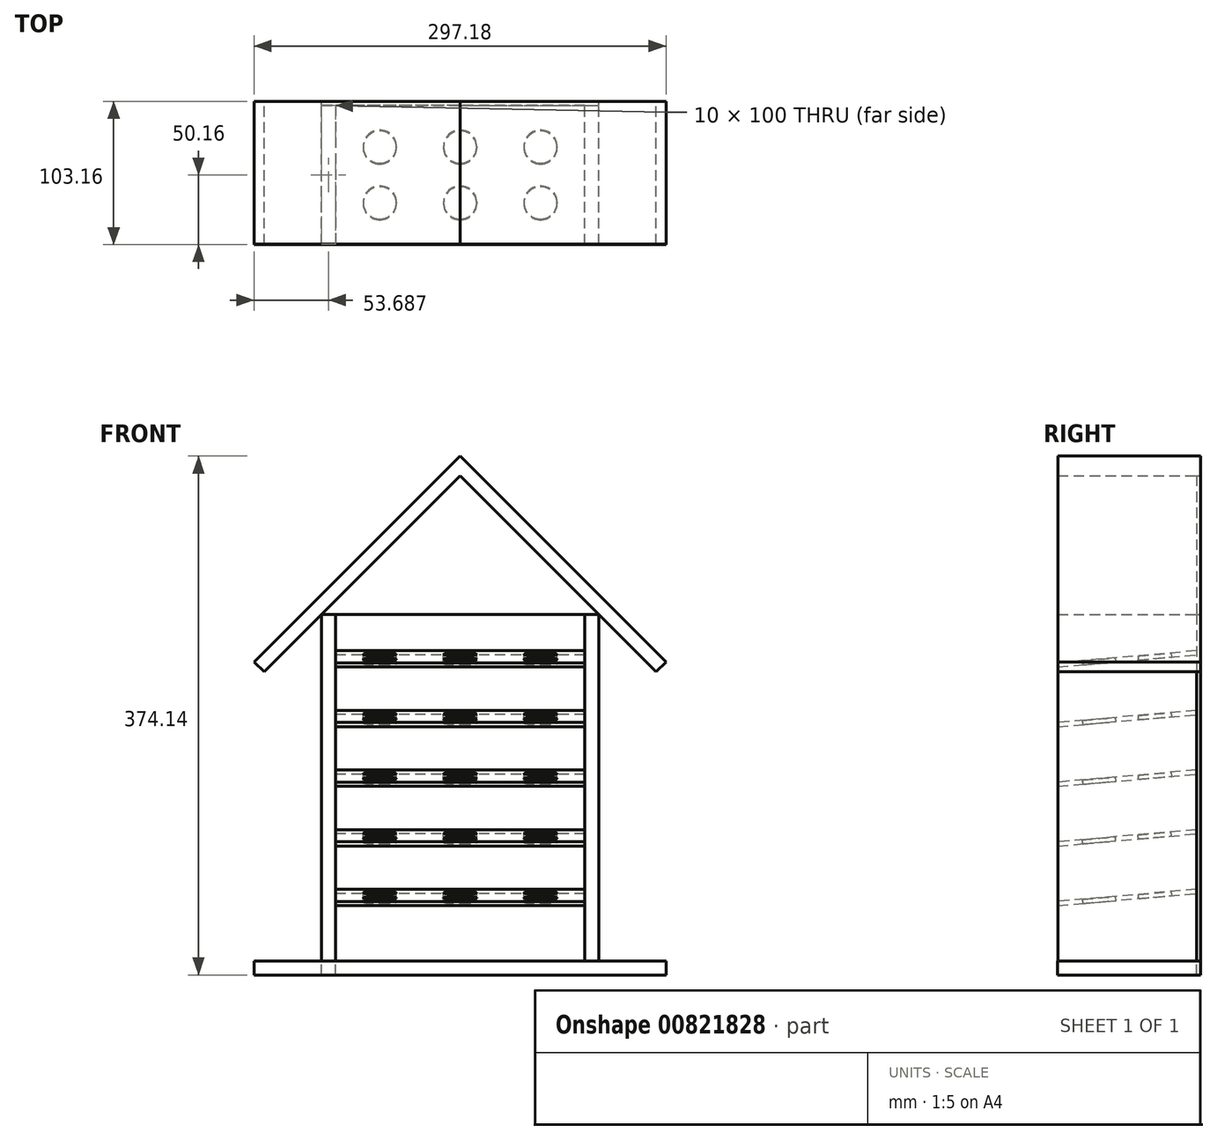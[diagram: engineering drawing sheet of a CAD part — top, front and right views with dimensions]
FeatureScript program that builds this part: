
annotation { "Feature Type Name" : "Feature", "Feature Type Description" : "" }
export const myFeature = defineFeature(function(context is Context, id is Id, definition is map)
    precondition{}
    {
        {
            var Q0;
            Q0=qCreatedBy(makeId("Front.planeOp"),FACE);
            var sketch = newSketch(context, id + "F0", { "sketchPlane" : qUnion([Q0])});
            skLineSegment(sketch, "E0.bottom", {"start": v(-116.5, 263.5) * mm, "end": v(83.5, 263.5) * mm});
            skLineSegment(sketch, "E0.top", {"start": v(-116.5, 13.5) * mm, "end": v(83.5, 13.5) * mm});
            skLineSegment(sketch, "E0.left", {"start": v(-116.5, 263.5) * mm, "end": v(-116.5, 13.5) * mm});
            skLineSegment(sketch, "E0.right", {"start": v(83.5, 263.5) * mm, "end": v(83.5, 13.5) * mm});
            skLineSegment(sketch, "E1", {"start": v(-16.5, 363.5) * mm, "end": v(-157.91, 222.09) * mm});
            skLineSegment(sketch, "E2", {"start": v(-16.5, 13.5) * mm, "end": v(-16.5, 535.12) * mm, "construction": true});
            skLineSegment(sketch, "E3", {"start": v(-157.91, 222.09) * mm, "end": v(-164.99, 229.16) * mm});
            skLineSegment(sketch, "E4", {"start": v(-164.99, 229.16) * mm, "end": v(-16.5, 377.65) * mm});
            skLineSegment(sketch, "E5.MirrorCS", {"start": v(132, 229.16) * mm, "end": v(-16.5, 377.65) * mm});
            skLineSegment(sketch, "E6.MirrorCS", {"start": v(-16.5, 363.5) * mm, "end": v(124.93, 222.09) * mm});
            skLineSegment(sketch, "E7.MirrorCS", {"start": v(124.93, 222.09) * mm, "end": v(132, 229.16) * mm});
            skSolve(sketch);
        }
        {
            var Q0;
            Q0=makeQuery(id+"F0.imprint","IMPRINT",FACE,{"disambiguationData":[TD([[makeQuery(id+"F0.imprint","IMPRINT",EDGE,{"derivedFrom":sQuery(id+"F0.wireOp",EDGE,"E0.bottom")}),-1.0]])]});
            extrude(context, id + "F1", {"entities" : qUnion([Q0]), "depth" : 3 * mm, "offsetDistance" : 25 * mm});
        }
        {
            var Q0;
            Q0=makeQuery(id+"F1.opExtrude","CAP_FACE",FACE,{"disambiguationData":[OSD([sQuery(id+"F0.wireOp",EDGE,"E0.bottom"),sQuery(id+"F0.wireOp",EDGE,"E0.top"),sQuery(id+"F0.wireOp",EDGE,"E0.left"),sQuery(id+"F0.wireOp",EDGE,"E0.right")])],"isStart":false});
            var sketch = newSketch(context, id + "F2", { "sketchPlane" : qUnion([Q0])});
            skLineSegment(sketch, "E8.bottom", {"start": v(-116.5, 263.5) * mm, "end": v(-106.5, 263.5) * mm});
            skLineSegment(sketch, "E8.top", {"start": v(-116.5, 13.5) * mm, "end": v(-106.5, 13.5) * mm});
            skLineSegment(sketch, "E8.left", {"start": v(-116.5, 263.5) * mm, "end": v(-116.5, 13.5) * mm});
            skLineSegment(sketch, "E8.right", {"start": v(-106.5, 263.5) * mm, "end": v(-106.5, 13.5) * mm});
            skSolve(sketch);
        }
        {
            var Q0;
            Q0=makeQuery(id+"F2.imprint","IMPRINT",FACE,{"disambiguationData":[TD([[makeQuery(id+"F2.imprint","IMPRINT",EDGE,{"derivedFrom":sQuery(id+"F2.wireOp",EDGE,"E8.bottom")}),-1.0]])]});
            extrude(context, id + "F3", {"entities" : qUnion([Q0]), "depth" : 100 * mm, "offsetDistance" : 25 * mm});
        }
        {
            var Q0;
            Q0=makeQuery(id+"F1.opExtrude","CAP_FACE",FACE,{"disambiguationData":[OSD([sQuery(id+"F0.wireOp",EDGE,"E0.bottom"),sQuery(id+"F0.wireOp",EDGE,"E0.top"),sQuery(id+"F0.wireOp",EDGE,"E0.left"),sQuery(id+"F0.wireOp",EDGE,"E0.right")])],"isStart":false});
            var sketch = newSketch(context, id + "F4", { "sketchPlane" : qUnion([Q0])});
            skLineSegment(sketch, "E9.bottom", {"start": v(83.5, 263.5) * mm, "end": v(73.5, 263.5) * mm});
            skLineSegment(sketch, "E9.top", {"start": v(83.5, 13.5) * mm, "end": v(73.5, 13.5) * mm});
            skLineSegment(sketch, "E9.left", {"start": v(83.5, 263.5) * mm, "end": v(83.5, 13.5) * mm});
            skLineSegment(sketch, "E9.right", {"start": v(73.5, 263.5) * mm, "end": v(73.5, 13.5) * mm});
            skSolve(sketch);
        }
        {
            var Q0;
            Q0=makeQuery(id+"F4.imprint","IMPRINT",FACE,{"disambiguationData":[TD([[makeQuery(id+"F4.imprint","IMPRINT",EDGE,{"derivedFrom":sQuery(id+"F4.wireOp",EDGE,"E9.bottom")}),-1.0]])]});
            extrude(context, id + "F5", {"entities" : qUnion([Q0]), "depth" : 100 * mm, "offsetDistance" : 25 * mm});
        }
        {
            var Q0;
            Q0=makeQuery(id+"F3.opExtrude","SWEPT_FACE",FACE,{"disambiguationData":[OSD([sQuery(id+"F2.wireOp",EDGE,"E8.right")])]});
            var sketch = newSketch(context, id + "F6", { "sketchPlane" : qUnion([Q0])});
            skLineSegment(sketch, "E10", {"start": v(-103, 53.5) * mm, "end": v(-3, 62.26) * mm});
            skLineSegment(sketch, "E11", {"start": v(-3, 62.26) * mm, "end": v(-3, 65.26) * mm});
            skLineSegment(sketch, "E12", {"start": v(-3, 65.26) * mm, "end": v(-103, 56.5) * mm});
            skLineSegment(sketch, "E13", {"start": v(-103, 56.5) * mm, "end": v(-103, 53.5) * mm});
            skLineSegment(sketch, "E14", {"start": v(-103, 96.5) * mm, "end": v(-3, 105.26) * mm});
            skLineSegment(sketch, "E15", {"start": v(-3, 105.26) * mm, "end": v(-3, 108.26) * mm});
            skLineSegment(sketch, "E16", {"start": v(-3, 108.26) * mm, "end": v(-103, 99.5) * mm});
            skLineSegment(sketch, "E17", {"start": v(-103, 99.5) * mm, "end": v(-103, 96.5) * mm});
            skLineSegment(sketch, "E18", {"start": v(-103, 139.5) * mm, "end": v(-3, 148.26) * mm});
            skLineSegment(sketch, "E19", {"start": v(-3, 148.26) * mm, "end": v(-3, 151.26) * mm});
            skLineSegment(sketch, "E20", {"start": v(-3, 151.26) * mm, "end": v(-103, 142.5) * mm});
            skLineSegment(sketch, "E21", {"start": v(-103, 142.5) * mm, "end": v(-103, 139.5) * mm});
            skLineSegment(sketch, "E22", {"start": v(-103, 182.5) * mm, "end": v(-3, 191.26) * mm});
            skLineSegment(sketch, "E23", {"start": v(-3, 191.26) * mm, "end": v(-3, 194.26) * mm});
            skLineSegment(sketch, "E24", {"start": v(-3, 194.26) * mm, "end": v(-103, 185.5) * mm});
            skLineSegment(sketch, "E25", {"start": v(-103, 185.5) * mm, "end": v(-103, 182.5) * mm});
            skLineSegment(sketch, "E26", {"start": v(-103, 225.5) * mm, "end": v(-3, 234.26) * mm});
            skLineSegment(sketch, "E27", {"start": v(-3, 234.26) * mm, "end": v(-3, 237.26) * mm});
            skLineSegment(sketch, "E28", {"start": v(-3, 237.26) * mm, "end": v(-103, 228.5) * mm});
            skLineSegment(sketch, "E29", {"start": v(-103, 228.5) * mm, "end": v(-103, 225.5) * mm});
            skSolve(sketch);
        }
        {
            var Q0;
            Q0=makeQuery(id+"F6.imprint","IMPRINT",FACE,{"disambiguationData":[TD([[makeQuery(id+"F6.imprint","IMPRINT",EDGE,{"derivedFrom":sQuery(id+"F6.wireOp",EDGE,"E10")}),1.0]])]});
            var Q1;
            Q1=makeQuery(id+"F6.imprint","IMPRINT",FACE,{"disambiguationData":[TD([[makeQuery(id+"F6.imprint","IMPRINT",EDGE,{"derivedFrom":sQuery(id+"F6.wireOp",EDGE,"E14")}),1.0]])]});
            var Q2;
            Q2=makeQuery(id+"F6.imprint","IMPRINT",FACE,{"disambiguationData":[TD([[makeQuery(id+"F6.imprint","IMPRINT",EDGE,{"derivedFrom":sQuery(id+"F6.wireOp",EDGE,"E18")}),1.0]])]});
            var Q3;
            Q3=makeQuery(id+"F6.imprint","IMPRINT",FACE,{"disambiguationData":[TD([[makeQuery(id+"F6.imprint","IMPRINT",EDGE,{"derivedFrom":sQuery(id+"F6.wireOp",EDGE,"E22")}),1.0]])]});
            var Q4;
            Q4=makeQuery(id+"F6.imprint","IMPRINT",FACE,{"disambiguationData":[TD([[makeQuery(id+"F6.imprint","IMPRINT",EDGE,{"derivedFrom":sQuery(id+"F6.wireOp",EDGE,"E26")}),1.0]])]});
            extrude(context, id + "F7", {"entities" : qUnion([Q0, Q1, Q2, Q3, Q4]), "endBound" : BoundingType.UP_TO_NEXT, "depth" : 210 * mm, "offsetDistance" : 25 * mm});
        }
        {
            var Q0;
            Q0=makeQuery(id+"F7.opExtrude","SWEPT_FACE",FACE,{"disambiguationData":[OSD([sQuery(id+"F6.wireOp",EDGE,"E28")])]});
            var sketch = newSketch(context, id + "F8", { "sketchPlane" : qUnion([Q0])});
            skCircle(sketch, "E30", {"center": v(-74.5, -52.7) * mm, "radius": 12 * mm});
            skCircle(sketch, "E31", {"center": v(-74.5, -12.31) * mm, "radius": 12 * mm});
            skCircle(sketch, "E32", {"center": v(-16.5, -52.7) * mm, "radius": 12 * mm});
            skCircle(sketch, "E33", {"center": v(-16.5, -12.31) * mm, "radius": 12 * mm});
            skCircle(sketch, "E34", {"center": v(41.5, -12.31) * mm, "radius": 12 * mm});
            skCircle(sketch, "E35", {"center": v(41.5, -52.7) * mm, "radius": 12 * mm});
            skLineSegment(sketch, "E36", {"start": v(-16.5, 17.69) * mm, "end": v(-16.5, -82.7) * mm, "construction": true});
            skSolve(sketch);
        }
        {
            var Q0;
            Q0=makeQuery(id+"F8.imprint","IMPRINT",FACE,{"disambiguationData":[TD([[makeQuery(id+"F8.imprint","IMPRINT",EDGE,{"derivedFrom":sQuery(id+"F8.wireOp",EDGE,"E31")}),1.0]])]});
            var Q1;
            Q1=makeQuery(id+"F8.imprint","IMPRINT",FACE,{"disambiguationData":[TD([[makeQuery(id+"F8.imprint","IMPRINT",EDGE,{"derivedFrom":sQuery(id+"F8.wireOp",EDGE,"E30")}),1.0]])]});
            var Q2;
            Q2=makeQuery(id+"F8.imprint","IMPRINT",FACE,{"disambiguationData":[TD([[makeQuery(id+"F8.imprint","IMPRINT",EDGE,{"derivedFrom":sQuery(id+"F8.wireOp",EDGE,"E32")}),1.0]])]});
            var Q3;
            Q3=makeQuery(id+"F8.imprint","IMPRINT",FACE,{"disambiguationData":[TD([[makeQuery(id+"F8.imprint","IMPRINT",EDGE,{"derivedFrom":sQuery(id+"F8.wireOp",EDGE,"E33")}),1.0]])]});
            var Q4;
            Q4=makeQuery(id+"F8.imprint","IMPRINT",FACE,{"disambiguationData":[TD([[makeQuery(id+"F8.imprint","IMPRINT",EDGE,{"derivedFrom":sQuery(id+"F8.wireOp",EDGE,"E34")}),1.0]])]});
            var Q5;
            Q5=makeQuery(id+"F8.imprint","IMPRINT",FACE,{"disambiguationData":[TD([[makeQuery(id+"F8.imprint","IMPRINT",EDGE,{"derivedFrom":sQuery(id+"F8.wireOp",EDGE,"E35")}),1.0]])]});
            extrude(context, id + "F9", {"entities" : qUnion([Q0, Q1, Q2, Q3, Q4, Q5]), "operationType" : NewBodyOperationType.REMOVE, "endBound" : BoundingType.UP_TO_NEXT, "oppositeDirection" : true, "depth" : 25 * mm, "offsetDistance" : 25 * mm});
        }
        {
            var Q0;
            Q0=makeQuery(id+"F7.opExtrude","SWEPT_FACE",FACE,{"disambiguationData":[OSD([sQuery(id+"F6.wireOp",EDGE,"E24")])]});
            var sketch = newSketch(context, id + "F10", { "sketchPlane" : qUnion([Q0])});
            skCircle(sketch, "E37", {"center": v(-74.5, -56.44) * mm, "radius": 12 * mm});
            skCircle(sketch, "E38", {"center": v(-74.5, -16.06) * mm, "radius": 12 * mm});
            skCircle(sketch, "E39", {"center": v(-16.5, -56.44) * mm, "radius": 12 * mm});
            skCircle(sketch, "E40", {"center": v(-16.5, -16.06) * mm, "radius": 12 * mm});
            skCircle(sketch, "E41", {"center": v(41.5, -16.06) * mm, "radius": 12 * mm});
            skCircle(sketch, "E42", {"center": v(41.5, -56.44) * mm, "radius": 12 * mm});
            skLineSegment(sketch, "E43", {"start": v(-16.5, 13.94) * mm, "end": v(-16.5, -86.44) * mm, "construction": true});
            skSolve(sketch);
        }
        {
            var Q0;
            Q0=makeQuery(id+"F10.imprint","IMPRINT",FACE,{"disambiguationData":[TD([[makeQuery(id+"F10.imprint","IMPRINT",EDGE,{"derivedFrom":sQuery(id+"F10.wireOp",EDGE,"E38")}),1.0]])]});
            var Q1;
            Q1=makeQuery(id+"F10.imprint","IMPRINT",FACE,{"disambiguationData":[TD([[makeQuery(id+"F10.imprint","IMPRINT",EDGE,{"derivedFrom":sQuery(id+"F10.wireOp",EDGE,"E37")}),1.0]])]});
            var Q2;
            Q2=makeQuery(id+"F10.imprint","IMPRINT",FACE,{"disambiguationData":[TD([[makeQuery(id+"F10.imprint","IMPRINT",EDGE,{"derivedFrom":sQuery(id+"F10.wireOp",EDGE,"E39")}),1.0]])]});
            var Q3;
            Q3=makeQuery(id+"F10.imprint","IMPRINT",FACE,{"disambiguationData":[TD([[makeQuery(id+"F10.imprint","IMPRINT",EDGE,{"derivedFrom":sQuery(id+"F10.wireOp",EDGE,"E40")}),1.0]])]});
            var Q4;
            Q4=makeQuery(id+"F10.imprint","IMPRINT",FACE,{"disambiguationData":[TD([[makeQuery(id+"F10.imprint","IMPRINT",EDGE,{"derivedFrom":sQuery(id+"F10.wireOp",EDGE,"E41")}),1.0]])]});
            var Q5;
            Q5=makeQuery(id+"F10.imprint","IMPRINT",FACE,{"disambiguationData":[TD([[makeQuery(id+"F10.imprint","IMPRINT",EDGE,{"derivedFrom":sQuery(id+"F10.wireOp",EDGE,"E42")}),1.0]])]});
            extrude(context, id + "F11", {"entities" : qUnion([Q0, Q1, Q2, Q3, Q4, Q5]), "operationType" : NewBodyOperationType.REMOVE, "oppositeDirection" : true, "depth" : 25 * mm, "offsetDistance" : 25 * mm});
        }
        {
            var Q0;
            Q0=makeQuery(id+"F7.opExtrude","SWEPT_FACE",FACE,{"disambiguationData":[OSD([sQuery(id+"F6.wireOp",EDGE,"E20")])]});
            var sketch = newSketch(context, id + "F12", { "sketchPlane" : qUnion([Q0])});
            skCircle(sketch, "E44", {"center": v(-74.5, -60.19) * mm, "radius": 12 * mm});
            skCircle(sketch, "E45", {"center": v(-74.5, -19.8) * mm, "radius": 12 * mm});
            skCircle(sketch, "E46", {"center": v(-16.5, -60.19) * mm, "radius": 12 * mm});
            skCircle(sketch, "E47", {"center": v(-16.5, -19.8) * mm, "radius": 12 * mm});
            skCircle(sketch, "E48", {"center": v(41.5, -19.8) * mm, "radius": 12 * mm});
            skCircle(sketch, "E49", {"center": v(41.5, -60.19) * mm, "radius": 12 * mm});
            skLineSegment(sketch, "E50", {"start": v(-16.5, 10.2) * mm, "end": v(-16.5, -90.19) * mm, "construction": true});
            skSolve(sketch);
        }
        {
            var Q0;
            Q0=makeQuery(id+"F12.imprint","IMPRINT",FACE,{"disambiguationData":[TD([[makeQuery(id+"F12.imprint","IMPRINT",EDGE,{"derivedFrom":sQuery(id+"F12.wireOp",EDGE,"E45")}),1.0]])]});
            var Q1;
            Q1=makeQuery(id+"F12.imprint","IMPRINT",FACE,{"disambiguationData":[TD([[makeQuery(id+"F12.imprint","IMPRINT",EDGE,{"derivedFrom":sQuery(id+"F12.wireOp",EDGE,"E44")}),1.0]])]});
            var Q2;
            Q2=makeQuery(id+"F12.imprint","IMPRINT",FACE,{"disambiguationData":[TD([[makeQuery(id+"F12.imprint","IMPRINT",EDGE,{"derivedFrom":sQuery(id+"F12.wireOp",EDGE,"E46")}),1.0]])]});
            var Q3;
            Q3=makeQuery(id+"F12.imprint","IMPRINT",FACE,{"disambiguationData":[TD([[makeQuery(id+"F12.imprint","IMPRINT",EDGE,{"derivedFrom":sQuery(id+"F12.wireOp",EDGE,"E47")}),1.0]])]});
            var Q4;
            Q4=makeQuery(id+"F12.imprint","IMPRINT",FACE,{"disambiguationData":[TD([[makeQuery(id+"F12.imprint","IMPRINT",EDGE,{"derivedFrom":sQuery(id+"F12.wireOp",EDGE,"E48")}),1.0]])]});
            var Q5;
            Q5=makeQuery(id+"F12.imprint","IMPRINT",FACE,{"disambiguationData":[TD([[makeQuery(id+"F12.imprint","IMPRINT",EDGE,{"derivedFrom":sQuery(id+"F12.wireOp",EDGE,"E49")}),1.0]])]});
            extrude(context, id + "F13", {"entities" : qUnion([Q0, Q1, Q2, Q3, Q4, Q5]), "operationType" : NewBodyOperationType.REMOVE, "endBound" : BoundingType.UP_TO_NEXT, "oppositeDirection" : true, "depth" : 25 * mm, "offsetDistance" : 25 * mm});
        }
        {
            var Q0;
            Q0=makeQuery(id+"F7.opExtrude","SWEPT_FACE",FACE,{"disambiguationData":[OSD([sQuery(id+"F6.wireOp",EDGE,"E16")])]});
            var sketch = newSketch(context, id + "F14", { "sketchPlane" : qUnion([Q0])});
            skCircle(sketch, "E51", {"center": v(-74.5, -64.2) * mm, "radius": 12 * mm});
            skCircle(sketch, "E52", {"center": v(-74.5, -23.81) * mm, "radius": 12 * mm});
            skCircle(sketch, "E53", {"center": v(-16.5, -64.2) * mm, "radius": 12 * mm});
            skCircle(sketch, "E54", {"center": v(-16.5, -23.81) * mm, "radius": 12 * mm});
            skCircle(sketch, "E55", {"center": v(41.5, -23.81) * mm, "radius": 12 * mm});
            skCircle(sketch, "E56", {"center": v(41.5, -64.2) * mm, "radius": 12 * mm});
            skLineSegment(sketch, "E57", {"start": v(-16.5, 6.19) * mm, "end": v(-16.5, -94.2) * mm, "construction": true});
            skSolve(sketch);
        }
        {
            var Q0;
            Q0=makeQuery(id+"F14.imprint","IMPRINT",FACE,{"disambiguationData":[TD([[makeQuery(id+"F14.imprint","IMPRINT",EDGE,{"derivedFrom":sQuery(id+"F14.wireOp",EDGE,"E52")}),1.0]])]});
            var Q1;
            Q1=makeQuery(id+"F14.imprint","IMPRINT",FACE,{"disambiguationData":[TD([[makeQuery(id+"F14.imprint","IMPRINT",EDGE,{"derivedFrom":sQuery(id+"F14.wireOp",EDGE,"E51")}),1.0]])]});
            var Q2;
            Q2=makeQuery(id+"F14.imprint","IMPRINT",FACE,{"disambiguationData":[TD([[makeQuery(id+"F14.imprint","IMPRINT",EDGE,{"derivedFrom":sQuery(id+"F14.wireOp",EDGE,"E54")}),1.0]])]});
            var Q3;
            Q3=makeQuery(id+"F14.imprint","IMPRINT",FACE,{"disambiguationData":[TD([[makeQuery(id+"F14.imprint","IMPRINT",EDGE,{"derivedFrom":sQuery(id+"F14.wireOp",EDGE,"E53")}),1.0]])]});
            var Q4;
            Q4=makeQuery(id+"F14.imprint","IMPRINT",FACE,{"disambiguationData":[TD([[makeQuery(id+"F14.imprint","IMPRINT",EDGE,{"derivedFrom":sQuery(id+"F14.wireOp",EDGE,"E55")}),1.0]])]});
            var Q5;
            Q5=makeQuery(id+"F14.imprint","IMPRINT",FACE,{"disambiguationData":[TD([[makeQuery(id+"F14.imprint","IMPRINT",EDGE,{"derivedFrom":sQuery(id+"F14.wireOp",EDGE,"E56")}),1.0]])]});
            extrude(context, id + "F15", {"entities" : qUnion([Q0, Q1, Q2, Q3, Q4, Q5]), "operationType" : NewBodyOperationType.REMOVE, "endBound" : BoundingType.UP_TO_NEXT, "oppositeDirection" : true, "depth" : 25 * mm, "offsetDistance" : 25 * mm});
        }
        {
            var Q0;
            Q0=makeQuery(id+"F7.opExtrude","SWEPT_FACE",FACE,{"disambiguationData":[OSD([sQuery(id+"F6.wireOp",EDGE,"E12")])]});
            var sketch = newSketch(context, id + "F16", { "sketchPlane" : qUnion([Q0])});
            skCircle(sketch, "E58", {"center": v(-74.5, -67.68) * mm, "radius": 12 * mm});
            skCircle(sketch, "E59", {"center": v(-74.5, -27.3) * mm, "radius": 12 * mm});
            skCircle(sketch, "E60", {"center": v(-16.5, -67.68) * mm, "radius": 12 * mm});
            skCircle(sketch, "E61", {"center": v(-16.5, -27.3) * mm, "radius": 12 * mm});
            skCircle(sketch, "E62", {"center": v(41.5, -27.3) * mm, "radius": 12 * mm});
            skCircle(sketch, "E63", {"center": v(41.5, -67.68) * mm, "radius": 12 * mm});
            skLineSegment(sketch, "E64", {"start": v(-16.5, 2.7) * mm, "end": v(-16.5, -97.68) * mm, "construction": true});
            skSolve(sketch);
        }
        {
            var Q0;
            Q0=makeQuery(id+"F16.imprint","IMPRINT",FACE,{"disambiguationData":[TD([[makeQuery(id+"F16.imprint","IMPRINT",EDGE,{"derivedFrom":sQuery(id+"F16.wireOp",EDGE,"E59")}),1.0]])]});
            var Q1;
            Q1=makeQuery(id+"F16.imprint","IMPRINT",FACE,{"disambiguationData":[TD([[makeQuery(id+"F16.imprint","IMPRINT",EDGE,{"derivedFrom":sQuery(id+"F16.wireOp",EDGE,"E58")}),1.0]])]});
            var Q2;
            Q2=makeQuery(id+"F16.imprint","IMPRINT",FACE,{"disambiguationData":[TD([[makeQuery(id+"F16.imprint","IMPRINT",EDGE,{"derivedFrom":sQuery(id+"F16.wireOp",EDGE,"E60")}),1.0]])]});
            var Q3;
            Q3=makeQuery(id+"F16.imprint","IMPRINT",FACE,{"disambiguationData":[TD([[makeQuery(id+"F16.imprint","IMPRINT",EDGE,{"derivedFrom":sQuery(id+"F16.wireOp",EDGE,"E61")}),1.0]])]});
            var Q4;
            Q4=makeQuery(id+"F16.imprint","IMPRINT",FACE,{"disambiguationData":[TD([[makeQuery(id+"F16.imprint","IMPRINT",EDGE,{"derivedFrom":sQuery(id+"F16.wireOp",EDGE,"E62")}),1.0]])]});
            var Q5;
            Q5=makeQuery(id+"F16.imprint","IMPRINT",FACE,{"disambiguationData":[TD([[makeQuery(id+"F16.imprint","IMPRINT",EDGE,{"derivedFrom":sQuery(id+"F16.wireOp",EDGE,"E63")}),1.0]])]});
            extrude(context, id + "F17", {"entities" : qUnion([Q0, Q1, Q2, Q3, Q4, Q5]), "operationType" : NewBodyOperationType.REMOVE, "endBound" : BoundingType.UP_TO_NEXT, "oppositeDirection" : true, "depth" : 25 * mm, "offsetDistance" : 25 * mm});
        }
        {
            var Q0;
            {var subQ0=sQuery(id+"F0.wireOp",EDGE,"E3");Q0=makeQuery(id+"F0.imprint","IMPRINT",FACE,{"disambiguationData":[TD([[makeQuery(id+"F0.imprint","IMPRINT",EDGE,{"derivedFrom":subQ0}),-1.0]])]});}
            extrude(context, id + "F18", {"entities" : qUnion([Q0]), "depth" : 103 * mm, "offsetDistance" : 25 * mm});
        }
        {
            var Q0;
            Q0=makeQuery(id+"F1.opExtrude","SWEPT_FACE",FACE,{"disambiguationData":[OSD([sQuery(id+"F0.wireOp",EDGE,"E0.bottom")])]});
            extrude(context, id + "F19", {"entities" : qUnion([Q0]), "endBound" : BoundingType.UP_TO_NEXT, "depth" : 25 * mm, "offsetDistance" : 25 * mm});
        }
        {
            var Q0;
            Q0=makeQuery(id+"F3.opExtrude","SWEPT_FACE",FACE,{"disambiguationData":[OSD([sQuery(id+"F2.wireOp",EDGE,"E8.top")])]});
            var sketch = newSketch(context, id + "F20", { "sketchPlane" : qUnion([Q0])});
            skPoint(sketch, "E65.0", {"position": v(-164.99, 103) * mm});
            skPoint(sketch, "E66.0", {"position": v(132, 0) * mm});
            skLineSegment(sketch, "E67.bottom", {"start": v(-165.18, 103.16) * mm, "end": v(132, 103.16) * mm});
            skLineSegment(sketch, "E67.top", {"start": v(-165.18, 0) * mm, "end": v(132, 0) * mm});
            skLineSegment(sketch, "E67.left", {"start": v(-165.18, 103.16) * mm, "end": v(-165.18, 0) * mm});
            skLineSegment(sketch, "E67.right", {"start": v(132, 103.16) * mm, "end": v(132, 0) * mm});
            skSolve(sketch);
        }
        {
            var Q0;
            Q0=makeQuery(id+"F20.imprint","IMPRINT",FACE,{"disambiguationData":[TD([[makeQuery(id+"F20.imprint","IMPRINT",EDGE,{"derivedFrom":sQuery(id+"F20.wireOp",EDGE,"E67.bottom")}),-1.0]])]});
            extrude(context, id + "F21", {"entities" : qUnion([Q0]), "depth" : 10 * mm, "offsetDistance" : 25 * mm});
        }
    });
